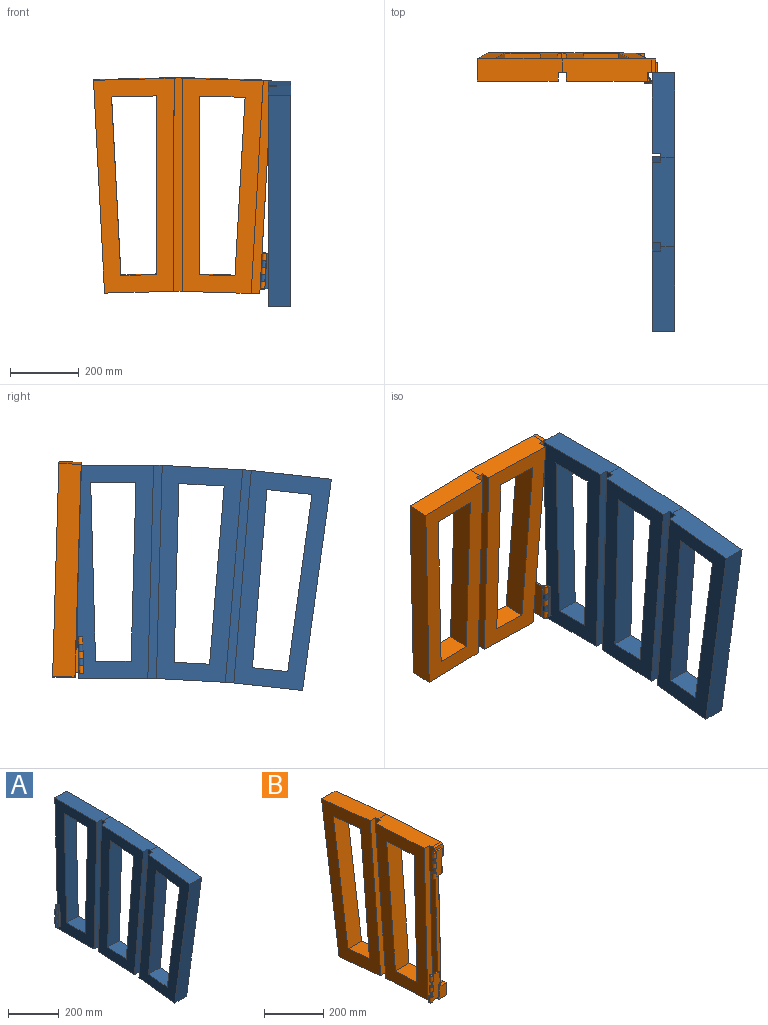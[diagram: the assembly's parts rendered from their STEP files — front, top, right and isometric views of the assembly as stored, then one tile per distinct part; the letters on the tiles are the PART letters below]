
ASSEMBLY  parts=2 mates=1
PART A: 112 faces, bbox 87.5x751.7x655.3 mm
  f0: plane 247x65mm, normal (0,0,1), area 15742.4mm2, adj f2,f9,f10,f16,f102,f105
  f1: plane 131.74x65mm, normal (0,0,-1), area 8563.1mm2, adj f2,f8,f34,f105
  f2: plane 751.66x655.33mm, normal (1,0,0), area 226323.8mm2, adj f0,f1,f8,f11,f12,f13,f14,f15
  f3: plane 101.22x6.25mm, normal (-1,0,0), area 348.1mm2, adj f7,f35,f95,f104
  f4: cylinder r=8mm len=20.42mm, axis (-0.06,-0.03,-1), area 64.6mm2, adj f7,f21,f31,f85,f104
  f5: plane 7.99x7.2mm, normal (0.06,0.03,1), area 47mm2, adj f6,f104
  f6: cylinder r=4mm len=20.78mm, axis (0.06,0.03,1), area 507.1mm2, adj f5,f31,f104
  f7: plane 101.22x6.81mm, normal (0,-1,0.03), area 444.6mm2, adj f3,f4,f22,f23,f25,f26,f27,f28
  f8: plane 519.91x65mm, normal (0,1,0.03), area 33806.6mm2, adj f1,f2,f100,f105
  f9: plane 619.91x25mm, normal (0,-1,-0.03), area 15503.5mm2, adj f0,f10,f17,f105
  f10: plane 620.59x41.85mm, normal (-1,0,0), area 15503.5mm2, adj f0,f9,f17,f63,f79,f102
  f11: plane 515.3x70.48mm, normal (0,0.99,0.14), area 33806.6mm2, adj f2,f15,f33,f37
  f12: plane 245.54x65mm, normal (0,-0.11,0.99), area 15742.4mm2, adj f2,f13,f37,f47,f81,f102
  f13: plane 614.42x84.04mm, normal (0,-0.99,-0.14), area 40309mm2, adj f2,f12,f14,f37
  f14: plane 212.03x65mm, normal (0,0.11,-0.99), area 13551mm2, adj f2,f13,f37,f47,f79,f81
  f15: plane 102.85x65mm, normal (0,-0.11,0.99), area 6725.2mm2, adj f2,f11,f37,f80
  f16: plane 619.91x65mm, normal (0,1,-0.03), area 29685.3mm2, adj f0,f2,f17,f19,f32,f36,f53,f61
  f17: plane 213.29x65mm, normal (0,0,-1), area 13551mm2, adj f2,f9,f10,f16,f79,f105
  f18: plane 103.26x27mm, normal (0,1,-0.03), area 2747.6mm2, adj f19,f36,f61,f84
  f19: plane 55x14.58mm, normal (0.06,0.03,1), area 636.6mm2, adj f16,f18,f44,f61,f73,f74,f84,f105
  f20: plane 520.59x39.13mm, normal (1,0,0), area 13002.5mm2, adj f49,f51,f56,f58,f59,f99
  f21: plane 103.1x35.77mm, normal (0,1,-0.03), area 3095.4mm2, adj f4,f22,f23,f24,f26,f27,f28,f29
  f22: cylinder r=7mm len=21.16mm, axis (0.06,0.03,1), area 827.6mm2, adj f7,f21,f27,f31
  f23: cylinder r=7mm len=21.16mm, axis (0.06,0.03,1), area 827.6mm2, adj f7,f21,f28,f29
  f24: plane 101.48x5.76mm, normal (1,0,-0.06), area 304.8mm2, adj f21,f32,f52,f53
  f25: plane 0.13x0.07mm, normal (-0.06,-0.03,-1), area 0mm2, adj f7,f30,f90
  f26: cylinder r=8mm len=20.42mm, axis (-0.06,-0.03,-1), area 64.7mm2, adj f7,f21,f27,f28
  f27: plane 14.91x14mm, normal (-0.06,-0.03,-1), area 106.9mm2, adj f7,f21,f22,f26,f98
  f28: plane 14.91x14mm, normal (0.06,0.03,1), area 106.9mm2, adj f7,f21,f23,f26,f98
  f29: plane 14.91x14mm, normal (-0.06,-0.03,-1), area 106.9mm2, adj f7,f21,f23,f30,f97
  f30: cylinder r=8mm len=20.42mm, axis (-0.06,-0.03,-1), area 64.7mm2, adj f7,f21,f25,f29,f32
  f31: plane 14.91x14mm, normal (0.06,0.03,1), area 106.9mm2, adj f4,f6,f7,f21,f22
  f32: plane 36.71x11.05mm, normal (0.06,0.03,1), area 313.1mm2, adj f16,f21,f24,f30,f52,f53,f90
  f33: plane 130.96x65mm, normal (0,0.11,-0.99), area 8563.1mm2, adj f2,f11,f37,f80
  f34: plane 519.91x65mm, normal (0,-1,0.03), area 33806.6mm2, adj f1,f2,f100,f105
  f35: plane 6.71x3.51mm, normal (0.06,0.03,1), area 23.5mm2, adj f3,f7,f90,f95
  f36: plane 55x14.58mm, normal (-0.06,-0.03,-1), area 619.3mm2, adj f16,f18,f44,f61,f73,f74,f84,f105
  f37: plane 639.87x283.63mm, normal (-1,0,0), area 73774mm2, adj f11,f12,f13,f14,f15,f33,f47,f80
  f38: plane 520.41x67.29mm, normal (1,0,0), area 13002.5mm2, adj f48,f50,f54,f55,f57,f60
  f39: cylinder r=4mm len=20.78mm, axis (0.06,0.03,1), area 510.7mm2, adj f69,f70
  f40: cylinder r=4mm len=20.78mm, axis (0.06,0.03,1), area 510.7mm2, adj f41,f68
  f41: plane 8x7.99mm, normal (-0.06,-0.03,-1), area 50.3mm2, adj f40
  f42: cylinder r=4mm len=20.78mm, axis (0.06,0.03,1), area 510.7mm2, adj f43,f66
  f43: plane 8x7.99mm, normal (0.06,0.03,1), area 50.3mm2, adj f42
  f44: plane 101.78x6.69mm, normal (0,1,-0.03), area 387.3mm2, adj f19,f36,f73,f84
  f45: plane 101.48x5.76mm, normal (-1,0,0.06), area 304.8mm2, adj f46,f72,f75,f78
  f46: plane 103.37x34.64mm, normal (0,-1,0.03), area 3231.6mm2, adj f45,f72,f78,f86,f87,f88
  f47: plane 618.08x50.52mm, normal (0,1,0.08), area 15503.5mm2, adj f12,f14,f37,f81
  f48: plane 518.37x42.37mm, normal (0,-1,-0.08), area 13002.5mm2, adj f2,f38,f50,f60
  f49: plane 25x12.49mm, normal (0,-0.05,1), area 312.6mm2, adj f2,f20,f56,f99
  f50: plane 25x12.49mm, normal (0,-0.05,1), area 312.6mm2, adj f2,f38,f48,f54
  f51: plane 25x12.49mm, normal (0,0.05,-1), area 312.6mm2, adj f2,f20,f56,f58
  f52: plane 101.73x5.76mm, normal (0,1,-0.03), area 293.1mm2, adj f24,f32,f53
  f53: plane 102.03x13.76mm, normal (-1,0,0), area 1119.4mm2, adj f16,f24,f32,f52,f85
  f54: plane 25x12.43mm, normal (0,-0.11,0.99), area 312.6mm2, adj f2,f38,f50,f55
  f55: plane 518.37x42.37mm, normal (0,1,0.08), area 13002.5mm2, adj f2,f38,f54,f57
  f56: plane 519.91x25mm, normal (0,1,0.03), area 13002.5mm2, adj f2,f20,f49,f51
  f57: plane 25x12.43mm, normal (0,0.11,-0.99), area 312.6mm2, adj f2,f38,f55,f60
  f58: plane 25x12.5mm, normal (0,0,-1), area 312.6mm2, adj f2,f20,f51,f59
  f59: plane 519.91x25mm, normal (0,-1,-0.03), area 13002.5mm2, adj f2,f20,f58,f99
  f60: plane 25x12.49mm, normal (0,0.05,-1), area 312.6mm2, adj f2,f38,f48,f57
  f61: plane 102.12x17.26mm, normal (-1,0,0), area 1475.6mm2, adj f16,f18,f19,f36
  f62: plane 618.08x50.52mm, normal (0,-1,-0.08), area 15503.5mm2, adj f79,f81,f102,f103
  f63: plane 619.91x25mm, normal (0,1,0.03), area 15503.5mm2, adj f10,f79,f102,f103
  f64: plane 103.31x65mm, normal (0,-0.05,1), area 6725.2mm2, adj f2,f82,f83,f103
  f65: cylinder r=8mm len=20.42mm, axis (-0.06,-0.03,-1), area 64.7mm2, adj f66,f74,f75,f78
  f66: plane 14.91x14mm, normal (0.06,0.03,1), area 106.9mm2, adj f42,f65,f74,f75,f77
  f67: cylinder r=8mm len=20.42mm, axis (-0.06,-0.03,-1), area 64.7mm2, adj f68,f72,f74,f75
  f68: plane 14.91x14mm, normal (-0.06,-0.03,-1), area 106.9mm2, adj f40,f67,f74,f75,f76
  f69: plane 14.91x14mm, normal (0.06,0.03,1), area 106.9mm2, adj f39,f71,f74,f75,f76
  f70: plane 14.91x14mm, normal (-0.06,-0.03,-1), area 106.9mm2, adj f39,f71,f74,f75,f77
  f71: cylinder r=8mm len=20.42mm, axis (-0.06,-0.03,-1), area 64.7mm2, adj f69,f70,f74,f75
  f72: plane 9.71x6.01mm, normal (-0.06,-0.03,-1), area 56.3mm2, adj f45,f46,f67,f74,f75,f105
  f73: plane 101.48x5.76mm, normal (1,0,-0.06), area 304.8mm2, adj f19,f36,f44,f74
  f74: plane 103.1x35.77mm, normal (0,1,-0.03), area 3095.4mm2, adj f19,f36,f65,f66,f67,f68,f69,f70
  f75: plane 101.4x5.86mm, normal (0,-1,0.03), area 55.4mm2, adj f45,f65,f66,f67,f68,f69,f70,f71
  f76: cylinder r=7mm len=21.16mm, axis (0.06,0.03,1), area 827.6mm2, adj f68,f69,f74,f75
  f77: cylinder r=7mm len=21.16mm, axis (0.06,0.03,1), area 827.6mm2, adj f66,f70,f74,f75
  f78: plane 6x3.95mm, normal (0.06,0.03,1), area 21.7mm2, adj f45,f46,f65,f74,f75,f105
  f79: plane 225.46x65mm, normal (0,0.05,-1), area 14051.2mm2, adj f2,f10,f14,f17,f62,f63,f81,f103
  f80: plane 518.37x65mm, normal (0,-1,-0.08), area 33806.6mm2, adj f2,f15,f33,f37
  f81: plane 620.11x75.44mm, normal (-1,0,0), area 15503.5mm2, adj f12,f14,f47,f62,f79,f102
  f82: plane 519.91x65mm, normal (0,-1,-0.03), area 33806.6mm2, adj f2,f64,f101,f103
  f83: plane 518.37x65mm, normal (0,1,0.08), area 33806.6mm2, adj f2,f64,f101,f103
  f84: plane 101.82x6.27mm, normal (1,0,0), area 356.2mm2, adj f18,f19,f36,f44
  f85: plane 30.95x10.46mm, normal (-0.06,-0.03,-1), area 249.6mm2, adj f4,f16,f21,f53,f94,f104
  f86: plane 101.74x3.27mm, normal (-1,0,0), area 50.9mm2, adj f46,f87,f88,f89
  f87: plane 25x1.43mm, normal (0.06,0.03,1), area 12.5mm2, adj f46,f86,f89,f105
  f88: plane 25x1.43mm, normal (-0.06,-0.03,-1), area 12.5mm2, adj f46,f86,f89,f105
  f89: plane 103.15x25mm, normal (0,1,-0.03), area 2544.1mm2, adj f86,f87,f88,f105
  f90: plane 14.55x2.39mm, normal (-1,0,0.06), area 29mm2, adj f16,f25,f32,f35,f91,f95
  f91: plane 14.98x14.52mm, normal (0.06,0.03,1), area 217.5mm2, adj f16,f90,f92,f95
  f92: plane 105.6x17.36mm, normal (1,0,-0.06), area 1507.3mm2, adj f16,f91,f93,f95,f104
  f93: plane 14.98x8.53mm, normal (-0.06,-0.03,-1), area 121.5mm2, adj f16,f92,f94,f104
  f94: plane 10.5x2.23mm, normal (-1,0,0.06), area 19mm2, adj f16,f85,f93,f104
  f95: plane 99.24x21.8mm, normal (0,1,-0.03), area 1870.5mm2, adj f3,f35,f90,f91,f92,f104
  f96: plane 8x7.99mm, normal (-0.06,-0.03,-1), area 50.3mm2, adj f97
  f97: cylinder r=4mm len=20.78mm, axis (0.06,0.03,1), area 510.7mm2, adj f29,f96
  f98: cylinder r=4mm len=20.78mm, axis (0.06,0.03,1), area 510.7mm2, adj f27,f28
  f99: plane 25x12.5mm, normal (0,0,1), area 312.6mm2, adj f2,f20,f49,f59
  f100: plane 103.46x65mm, normal (0,0,1), area 6725.2mm2, adj f2,f8,f34,f105
  f101: plane 131.55x65mm, normal (0,0.05,-1), area 8563.1mm2, adj f2,f82,f83,f103
  f102: plane 259.12x65mm, normal (0,-0.05,1), area 16242.6mm2, adj f0,f2,f10,f12,f62,f63,f81,f103
  f103: plane 630.82x251.01mm, normal (-1,0,0), area 73774mm2, adj f62,f63,f64,f79,f82,f83,f101,f102
  f104: plane 16.22x7.01mm, normal (0,0.7,-0.72), area 138.7mm2, adj f3,f4,f5,f6,f7,f85,f92,f93
  f105: plane 619.91x234.5mm, normal (-1,0,0), area 72298.4mm2, adj f0,f1,f8,f9,f16,f17,f19,f34
  f106: plane 101.74x3.27mm, normal (1,0,0), area 50.9mm2, adj f108,f109,f110,f111
  f107: plane 101.74x3.27mm, normal (-1,0,0), area 50.9mm2, adj f108,f109,f110,f111
  f108: plane 103.26x27mm, normal (0,-1,0.03), area 2747.6mm2, adj f106,f107,f109,f110
  f109: plane 27x1.55mm, normal (-0.06,-0.03,-1), area 13.5mm2, adj f106,f107,f108,f111
  f110: plane 27x1.55mm, normal (0.06,0.03,1), area 13.5mm2, adj f106,f107,f108,f111
  f111: plane 103.26x27mm, normal (0,1,-0.03), area 2747.6mm2, adj f106,f107,f109,f110
PART B: 87 faces, bbox 88.7x547.6x655.3 mm
  f0: plane 212.03x65mm, normal (0,-0.11,-0.99), area 13551mm2, adj f2,f52,f53,f78,f80,f86
  f1: plane 102.85x65mm, normal (0,0.11,0.99), area 6725.2mm2, adj f2,f3,f4,f86
  f2: plane 655.33x534.03mm, normal (1,0,0), area 152549.8mm2, adj f0,f1,f3,f4,f5,f52,f54,f56
  f3: plane 518.37x65mm, normal (0,1,-0.08), area 33806.6mm2, adj f1,f2,f84,f86
  f4: plane 515.3x70.48mm, normal (0,-0.99,0.14), area 33806.6mm2, adj f1,f2,f84,f86
  f5: plane 519.91x65mm, normal (0,1,-0.03), area 33806.6mm2, adj f2,f79,f81,f83
  f6: plane 619.91x25mm, normal (0,-1,0.03), area 15503.5mm2, adj f7,f80,f82,f83
  f7: plane 620.59x41.85mm, normal (-1,0,0), area 15808.7mm2, adj f6,f11,f16,f17,f56,f57,f59,f76
  f8: cylinder r=7mm len=23.16mm, axis (0.06,0.03,1), area 915.6mm2, adj f11,f13,f16,f23,f27
  f9: cylinder r=7mm len=21.15mm, axis (0.06,0.03,1), area 827.6mm2, adj f11,f13,f20,f22
  f10: cylinder r=4mm len=20.78mm, axis (0.06,0.03,1), area 510.7mm2, adj f23,f28
  f11: plane 101.85x7.96mm, normal (0,1,-0.03), area 469.2mm2, adj f7,f8,f9,f14,f16,f17,f18,f19
  f12: plane 101.48x5.76mm, normal (1,0,-0.06), area 304.8mm2, adj f13,f16,f17,f29
  f13: plane 103.16x36.78mm, normal (0,-1,0.03), area 3115.9mm2, adj f8,f9,f12,f14,f16,f17,f18,f19
  f14: cylinder r=7mm len=23.16mm, axis (0.06,0.03,1), area 915.6mm2, adj f11,f13,f17,f19,f25
  f15: cylinder r=4mm len=20.78mm, axis (0.06,0.03,1), area 510.7mm2, adj f19,f26
  f16: plane 37.96x6.04mm, normal (-0.06,-0.03,-1), area 184.7mm2, adj f7,f8,f11,f12,f13,f29,f56,f73
  f17: plane 32.2x6.04mm, normal (0.06,0.03,1), area 184.7mm2, adj f7,f11,f12,f13,f14,f74,f76
  f18: cylinder r=8mm len=20.31mm, axis (-0.06,-0.03,-1), area 64.7mm2, adj f11,f13,f19,f20
  f19: plane 14.91x14mm, normal (-0.06,-0.03,-1), area 106.9mm2, adj f11,f13,f14,f15,f18
  f20: plane 14.91x14mm, normal (0.06,0.03,1), area 106.9mm2, adj f9,f11,f13,f18,f24
  f21: cylinder r=8mm len=20.31mm, axis (-0.06,-0.03,-1), area 64.7mm2, adj f11,f13,f22,f23
  f22: plane 14.91x14mm, normal (-0.06,-0.03,-1), area 106.9mm2, adj f9,f11,f13,f21,f24
  f23: plane 14.91x14mm, normal (0.06,0.03,1), area 106.9mm2, adj f8,f10,f11,f13,f21
  f24: cylinder r=4mm len=20.78mm, axis (0.06,0.03,1), area 510.7mm2, adj f20,f22
  f25: plane 14x13.98mm, normal (0.06,0.03,1), area 153.9mm2, adj f14
  f26: plane 8x7.99mm, normal (-0.06,-0.03,-1), area 50.3mm2, adj f15
  f27: plane 14x13.98mm, normal (-0.06,-0.03,-1), area 153.9mm2, adj f8
  f28: plane 8x7.99mm, normal (0.06,0.03,1), area 50.3mm2, adj f10
  f29: plane 101.73x5.76mm, normal (0,-1,0.03), area 293.1mm2, adj f12,f16,f74
  f30: plane 101.47x7.01mm, normal (0,1,-0.03), area 79.4mm2, adj f31,f32,f34,f38,f39,f40,f41,f42
  f31: cylinder r=7mm len=23.16mm, axis (0.06,0.03,1), area 915.6mm2, adj f30,f37,f38,f45,f49
  f32: cylinder r=7mm len=21.15mm, axis (0.06,0.03,1), area 827.6mm2, adj f30,f37,f42,f44
  f33: cylinder r=4mm len=20.78mm, axis (0.06,0.03,1), area 510.7mm2, adj f45,f50
  f34: cylinder r=7mm len=23.16mm, axis (0.06,0.03,1), area 915.6mm2, adj f30,f37,f39,f41,f47
  f35: plane 101.48x5.76mm, normal (1,0,-0.06), area 304.8mm2, adj f37,f38,f39,f51
  f36: cylinder r=4mm len=20.78mm, axis (0.06,0.03,1), area 510.7mm2, adj f41,f48
  f37: plane 103.16x36.78mm, normal (0,-1,0.03), area 3115.9mm2, adj f31,f32,f34,f35,f38,f39,f40,f41
  f38: plane 38.89x6.05mm, normal (-0.06,-0.03,-1), area 207.7mm2, adj f30,f31,f35,f37,f51,f56,f59,f60
  f39: plane 33.13x6.05mm, normal (0.06,0.03,1), area 190.4mm2, adj f30,f34,f35,f37,f51,f56,f59,f60
  f40: cylinder r=8mm len=20.31mm, axis (-0.06,-0.03,-1), area 64.7mm2, adj f30,f37,f41,f42
  f41: plane 14.91x14mm, normal (-0.06,-0.03,-1), area 106.9mm2, adj f30,f34,f36,f37,f40
  f42: plane 14.91x14mm, normal (0.06,0.03,1), area 106.9mm2, adj f30,f32,f37,f40,f46
  f43: cylinder r=8mm len=20.31mm, axis (-0.06,-0.03,-1), area 64.7mm2, adj f30,f37,f44,f45
  f44: plane 14.91x14mm, normal (-0.06,-0.03,-1), area 106.9mm2, adj f30,f32,f37,f43,f46
  f45: plane 14.91x14mm, normal (0.06,0.03,1), area 106.9mm2, adj f30,f31,f33,f37,f43
  f46: cylinder r=4mm len=20.78mm, axis (0.06,0.03,1), area 510.7mm2, adj f42,f44
  f47: plane 14x13.98mm, normal (0.06,0.03,1), area 153.9mm2, adj f34
  f48: plane 8x7.99mm, normal (-0.06,-0.03,-1), area 50.3mm2, adj f36
  f49: plane 14x13.98mm, normal (-0.06,-0.03,-1), area 153.9mm2, adj f31
  f50: plane 8x7.99mm, normal (0.06,0.03,1), area 50.3mm2, adj f33
  f51: plane 101.78x6.69mm, normal (0,-1,0.03), area 387.3mm2, adj f35,f38,f39,f60
  f52: plane 614.42x84.04mm, normal (0,0.99,-0.14), area 40309mm2, adj f0,f2,f85,f86
  f53: plane 620.11x75.44mm, normal (-1,0,0), area 15503.5mm2, adj f0,f58,f78,f80,f82,f85
  f54: plane 518.37x65mm, normal (0,-1,0.08), area 33806.6mm2, adj f2,f79,f81,f83
  f55: plane 520.59x39.13mm, normal (1,0,0), area 13002.5mm2, adj f56,f65,f66,f69,f71,f72,f73
  f56: plane 507.39x40mm, normal (0,-1,0.03), area 8552.5mm2, adj f2,f7,f16,f38,f39,f55,f57,f60
  f57: plane 40x12.5mm, normal (0,0,-1), area 500.2mm2, adj f2,f7,f56,f80
  f58: plane 618.08x50.52mm, normal (0,1,-0.08), area 15503.5mm2, adj f53,f80,f82,f83
  f59: plane 103.37x34.64mm, normal (0,1,-0.03), area 3231.6mm2, adj f7,f38,f39,f61
  f60: plane 101.81x5.77mm, normal (1,0,0), area 305.3mm2, adj f38,f39,f51,f56
  f61: plane 101.48x5.76mm, normal (-1,0,0.06), area 304.8mm2, adj f30,f38,f39,f59
  f62: plane 518.37x42.37mm, normal (0,1,-0.08), area 13002.5mm2, adj f2,f63,f64,f75
  f63: plane 25x12.49mm, normal (0,-0.05,-1), area 312.6mm2, adj f2,f62,f67,f75
  f64: plane 25x12.49mm, normal (0,0.05,1), area 312.6mm2, adj f2,f62,f68,f75
  f65: plane 25x12.49mm, normal (0,-0.05,-1), area 312.6mm2, adj f2,f55,f66,f69
  f66: plane 25x12.5mm, normal (0,0,-1), area 312.6mm2, adj f2,f55,f65,f73,f76
  f67: plane 25x12.43mm, normal (0,-0.11,-0.99), area 312.6mm2, adj f2,f63,f70,f75
  f68: plane 25x12.43mm, normal (0,0.11,0.99), area 312.6mm2, adj f2,f64,f70,f75
  f69: plane 519.91x25mm, normal (0,-1,0.03), area 13002.5mm2, adj f2,f55,f65,f71
  f70: plane 518.37x42.37mm, normal (0,-1,0.08), area 13002.5mm2, adj f2,f67,f68,f75
  f71: plane 25x12.49mm, normal (0,0.05,1), area 312.6mm2, adj f2,f55,f69,f72
  f72: plane 25x12.5mm, normal (0,0,1), area 312.6mm2, adj f2,f55,f56,f71
  f73: plane 64.22x15mm, normal (0,1,-0.03), area 957.3mm2, adj f16,f55,f66,f74
  f74: plane 101.81x5.77mm, normal (1,0,0), area 305.3mm2, adj f16,f17,f29,f73,f76
  f75: plane 520.41x67.29mm, normal (1,0,0), area 13002.5mm2, adj f62,f63,f64,f67,f68,f70
  f76: plane 50x40mm, normal (0,-1,0.03), area 849.6mm2, adj f2,f7,f17,f66,f74,f77
  f77: plane 40x12.5mm, normal (0,0,1), area 500.2mm2, adj f2,f7,f76,f82
  f78: plane 618.08x50.52mm, normal (0,-1,0.08), area 15503.5mm2, adj f0,f53,f85,f86
  f79: plane 103.31x65mm, normal (0,0.05,1), area 6725.2mm2, adj f2,f5,f54,f83
  f80: plane 225.46x65mm, normal (0,-0.05,-1), area 14051.2mm2, adj f0,f2,f6,f7,f53,f57,f58,f83
  f81: plane 131.55x65mm, normal (0,-0.05,-1), area 8563.1mm2, adj f2,f5,f54,f83
  f82: plane 259.12x65mm, normal (0,0.05,1), area 16242.6mm2, adj f2,f6,f7,f53,f58,f77,f83,f85
  f83: plane 630.82x251.01mm, normal (-1,0,0), area 73774mm2, adj f5,f6,f54,f58,f79,f80,f81,f82
  f84: plane 130.96x65mm, normal (0,-0.11,-0.99), area 8563.1mm2, adj f2,f3,f4,f86
  f85: plane 245.54x65mm, normal (0,0.11,0.99), area 15742.4mm2, adj f2,f52,f53,f78,f82,f86
  f86: plane 639.87x283.63mm, normal (-1,0,0), area 73774mm2, adj f0,f1,f3,f4,f52,f78,f84,f85
PLACE A at identity fixed
PLACE B rot(axis=(0.06,0.03,1),90.1deg) t=(93.99,107.75,-8.27)mm
MATE revolute B.f8 <-> A.f6  axis (0.06,0.03,1) through (10.91,109.42,309.45)mm
